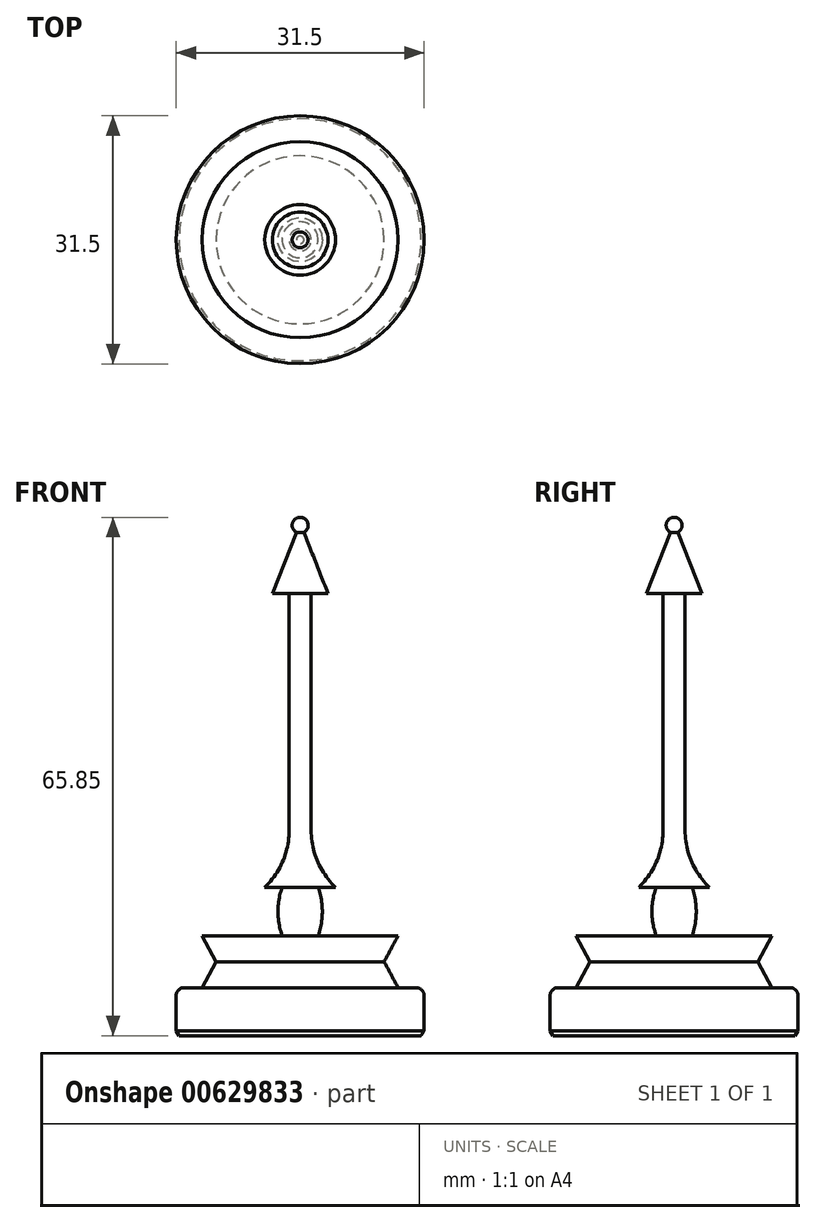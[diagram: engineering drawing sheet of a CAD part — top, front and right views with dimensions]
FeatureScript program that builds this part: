
annotation { "Feature Type Name" : "Feature", "Feature Type Description" : "" }
export const myFeature = defineFeature(function(context is Context, id is Id, definition is map)
    precondition{}
    {
        {
            var Q0;
            Q0=qCreatedBy(makeId("Front.planeOp"),FACE);
            var sketch = newSketch(context, id + "F0", { "sketchPlane" : qUnion([Q0])});
            skLineSegment(sketch, "E0.MirrorCS", {"start": v(15.37, 0) * mm, "end": v(15.75, 0.63) * mm});
            skLineSegment(sketch, "E1.MirrorCS", {"start": v(15.37, 0) * mm, "end": v(0, 0) * mm});
            skLineSegment(sketch, "E2", {"start": v(15.75, 0.64) * mm, "end": v(15.75, 5.08) * mm});
            skArc(sketch, "E3", {"start": v(15.75, 5.08) * mm, "mid": v(15.45, 5.8) * mm, "end": v(14.73, 6.1) * mm});
            skLineSegment(sketch, "E4", {"start": v(14.73, 6.1) * mm, "end": v(12.45, 6.1) * mm});
            skLineSegment(sketch, "E5", {"start": v(12.45, 12.7) * mm, "end": v(10.67, 9.4) * mm});
            skLineSegment(sketch, "E6", {"start": v(10.67, 9.4) * mm, "end": v(12.45, 6.1) * mm});
            skLineSegment(sketch, "E7", {"start": v(12.45, 12.7) * mm, "end": v(2.29, 12.7) * mm});
            skArc(sketch, "E8", {"start": v(0.48, 63.95) * mm, "mid": v(0.98, 65.08) * mm, "end": v(0, 65.85) * mm});
            skLineSegment(sketch, "E9", {"start": v(0, 65.85) * mm, "end": v(0, 0) * mm});
            skArc(sketch, "E10", {"start": v(2.29, 12.7) * mm, "mid": v(2.82, 15.77) * mm, "end": v(2.29, 18.85) * mm});
            skLineSegment(sketch, "E11", {"start": v(2.29, 18.85) * mm, "end": v(4.49, 18.85) * mm});
            skLineSegment(sketch, "E12", {"start": v(3.53, 56.2) * mm, "end": v(0.48, 63.95) * mm});
            skLineSegment(sketch, "E13", {"start": v(1.4, 56.2) * mm, "end": v(1.4, 26.1) * mm});
            skArc(sketch, "E14", {"start": v(1.4, 26.1) * mm, "mid": v(2.2, 22.16) * mm, "end": v(4.49, 18.85) * mm});
            skLineSegment(sketch, "E15", {"start": v(1.4, 56.2) * mm, "end": v(3.53, 56.2) * mm});
            skSolve(sketch);
        }
        {
            var Q0;
            Q0=makeQuery(id+"F0.imprint","IMPRINT",FACE,{"disambiguationData":[TD([[makeQuery(id+"F0.imprint","IMPRINT",EDGE,{"derivedFrom":sQuery(id+"F0.wireOp",EDGE,"E0.MirrorCS")}),1.0]])]});
            var Q1;
            Q1=sQuery(id+"F0.wireOp",EDGE,"E9");
            revolve(context, id + "F1", {"entities" : qUnion([Q0]), "axis" : qUnion([Q1]), "revolveType" : RevolveType.FULL});
        }
    });
